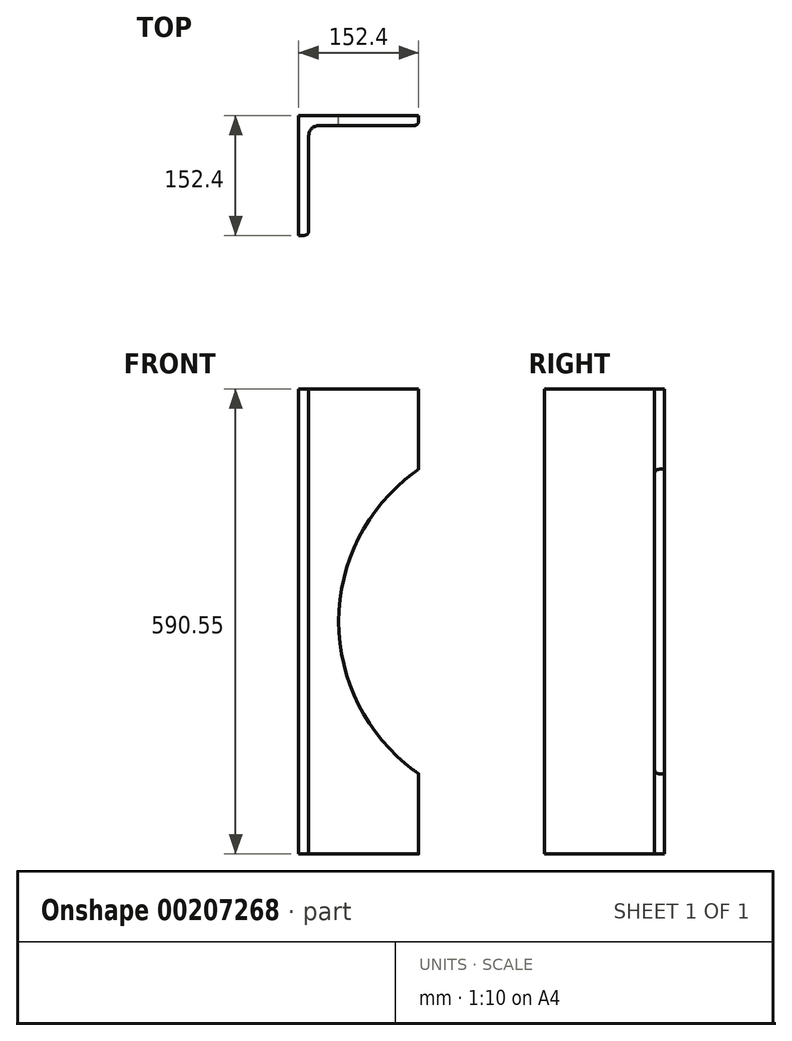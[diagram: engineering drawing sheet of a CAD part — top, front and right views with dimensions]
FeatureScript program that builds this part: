
annotation { "Feature Type Name" : "Feature", "Feature Type Description" : "" }
export const myFeature = defineFeature(function(context is Context, id is Id, definition is map)
    precondition{}
    {
        {
            var Q0;
            Q0=qCreatedBy(makeId("Top.planeOp"),FACE);
            var sketch = newSketch(context, id + "F0", { "sketchPlane" : qUnion([Q0])});
            skLineSegment(sketch, "E0", {"start": v(100.85, 50.43) * mm, "end": v(-51.55, 50.43) * mm});
            skLineSegment(sketch, "E1", {"start": v(-51.55, 50.43) * mm, "end": v(-51.55, -101.97) * mm});
            skLineSegment(sketch, "E2", {"start": v(-51.55, -101.97) * mm, "end": v(-45.2, -101.97) * mm});
            skLineSegment(sketch, "E3", {"start": v(-38.85, -95.62) * mm, "end": v(-38.85, 25.03) * mm});
            skLineSegment(sketch, "E4", {"start": v(-26.15, 37.73) * mm, "end": v(94.5, 37.73) * mm});
            skLineSegment(sketch, "E5", {"start": v(100.85, 44.08) * mm, "end": v(100.85, 50.43) * mm});
            skArc(sketch, "E6.filletArc", {"start": v(94.5, 37.73) * mm, "mid": v(99, 39.6) * mm, "end": v(100.85, 44.08) * mm});
            skArc(sketch, "E7.filletArc", {"start": v(-45.2, -101.97) * mm, "mid": v(-40.7, -100.1) * mm, "end": v(-38.85, -95.62) * mm});
            skArc(sketch, "E8.filletArc", {"start": v(-26.15, 37.73) * mm, "mid": v(-35.13, 34.01) * mm, "end": v(-38.85, 25.03) * mm});
            skSolve(sketch);
        }
        {
            var Q0;
            Q0=makeQuery(id+"F0.imprint","IMPRINT",FACE,{"disambiguationData":[TD([[makeQuery(id+"F0.imprint","IMPRINT",EDGE,{"derivedFrom":sQuery(id+"F0.wireOp",EDGE,"E0")}),1.0]])]});
            extrude(context, id + "F1", {"entities" : qUnion([Q0]), "depth" : 590.55 * mm});
        }
        {
            var Q0;
            Q0=makeQuery(id+"F1.opExtrude","SWEPT_FACE",FACE,{"disambiguationData":[OSD([sQuery(id+"F0.wireOp",EDGE,"E0")])]});
            var sketch = newSketch(context, id + "F2", { "sketchPlane" : qUnion([Q0])});
            skCircle(sketch, "E9", {"center": v(-234.2, 295.28) * mm, "radius": 234.95 * mm});
            skSolve(sketch);
        }
        {
            var Q0;
            {var subQ0=sQuery(id+"F2.wireOp",EDGE,"E9");var subQ1=makeQuery(id+"F1.opExtrude","SWEPT_EDGE",EDGE,{"disambiguationData":[OSD([sQuery(id+"F0.wireOp",EDGE,"E0"),sQuery(id+"F0.wireOp",EDGE,"E5")])]});var subQ2=makeQuery(id+"F2.imprint","INTERSECT",VERTEX,{"disambiguationData":[OD(0.0)],"derivedFrom":[subQ1,subQ0]});Q0=makeQuery(id+"F2.imprint","IMPRINT",FACE,{"disambiguationData":[TD([[makeQuery(id+"F2.imprint","IMPRINT",EDGE,{"disambiguationData":[TD([[subQ2,-1.0]])],"derivedFrom":subQ0}),1.0]])]});}
            extrude(context, id + "F3", {"entities" : qUnion([Q0]), "operationType" : NewBodyOperationType.REMOVE, "oppositeDirection" : true, "depth" : 25.4 * mm});
        }
    });
